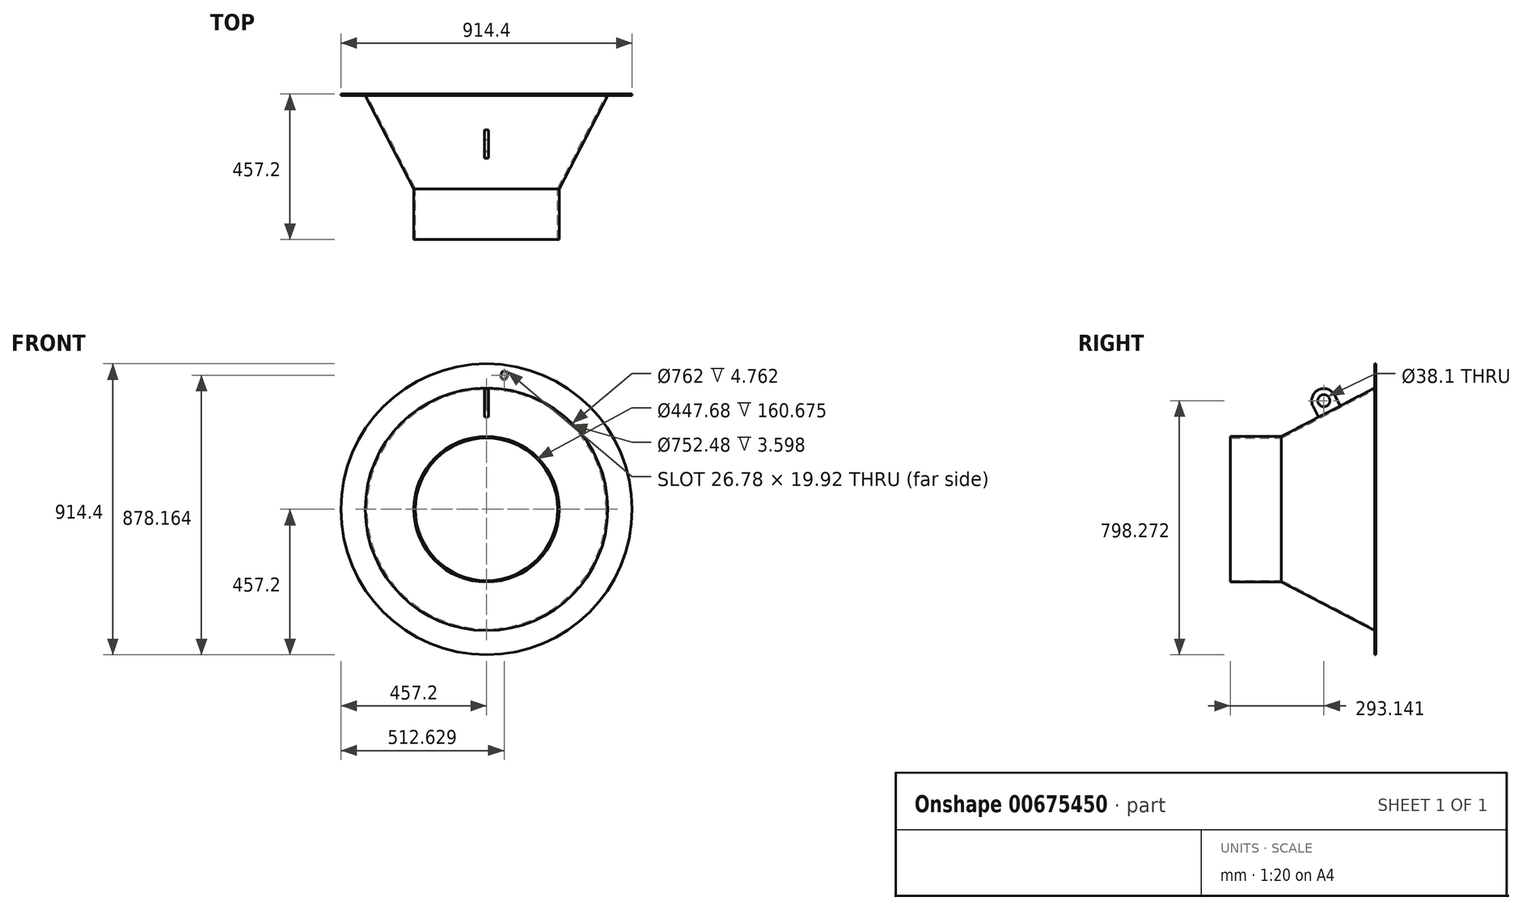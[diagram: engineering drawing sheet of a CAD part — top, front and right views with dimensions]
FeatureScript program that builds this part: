
annotation { "Feature Type Name" : "Feature", "Feature Type Description" : "" }
export const myFeature = defineFeature(function(context is Context, id is Id, definition is map)
    precondition{}
    {
        {
            var Q0;
            Q0=qCreatedBy(makeId("Front.planeOp"),FACE);
            var sketch = newSketch(context, id + "F0", { "sketchPlane" : qUnion([Q0])});
            skCircle(sketch, "E0", {"center": v(0, 0) * mm, "radius": 457.2 * mm});
            skCircle(sketch, "E1", {"center": v(0, 0) * mm, "radius": 428.63 * mm, "construction": true});
            skLineSegment(sketch, "E2", {"start": v(0, 0) * mm, "end": v(0, 611.06) * mm, "construction": true});
            skLineSegment(sketch, "E3", {"start": v(0, 0) * mm, "end": v(80.45, 611.06) * mm, "construction": true});
            skCircle(sketch, "E4", {"center": v(55.95, 424.96) * mm, "radius": 6.35 * mm});
            skCircle(sketch, "E5", {"center": v(0, 0) * mm, "radius": 381 * mm});
            skSolve(sketch);
        }
        {
            var Q0;
            Q0=qCreatedBy(makeId("Front.planeOp"),FACE);
            var sketch = newSketch(context, id + "F1", { "sketchPlane" : qUnion([Q0])});
            skCircle(sketch, "E6", {"center": v(0, 0) * mm, "radius": 420.69 * mm, "construction": true});
            skLineSegment(sketch, "E7.0", {"start": v(0, 0) * mm, "end": v(80.45, 611.06) * mm, "construction": true});
            skCircle(sketch, "E8", {"center": v(54.91, 417.09) * mm, "radius": 6.35 * mm});
            skSolve(sketch);
        }
        {
            var Q0;
            Q0=qCreatedBy(makeId("Front.planeOp"),FACE);
            var sketch = newSketch(context, id + "F2", { "sketchPlane" : qUnion([Q0])});
            skCircle(sketch, "E9.0", {"center": v(0, 0) * mm, "radius": 428.63 * mm, "construction": true});
            skCircle(sketch, "E10.0", {"center": v(0, 0) * mm, "radius": 420.69 * mm, "construction": true});
            skLineSegment(sketch, "E11.0", {"start": v(0, 0) * mm, "end": v(80.45, 611.06) * mm, "construction": true});
            skCircle(sketch, "E12", {"center": v(55.95, 424.96) * mm, "radius": 9.53 * mm});
            skCircle(sketch, "E13", {"center": v(54.91, 417.09) * mm, "radius": 9.53 * mm});
            skLineSegment(sketch, "E14", {"start": v(65.4, 423.71) * mm, "end": v(64.35, 415.85) * mm});
            skLineSegment(sketch, "E15", {"start": v(46.5, 426.2) * mm, "end": v(45.47, 418.33) * mm});
            skSolve(sketch);
        }
        {
            var Q0;
            Q0=qCreatedBy(makeId("Right.planeOp"),FACE);
            var sketch = newSketch(context, id + "F3", { "sketchPlane" : qUnion([Q0])});
            skLineSegment(sketch, "E16", {"start": v(190.49, 0) * mm, "end": v(-609.7, 0) * mm, "construction": true});
            skLineSegment(sketch, "E17", {"start": v(-4.76, 381) * mm, "end": v(-297.69, 228.6) * mm});
            skLineSegment(sketch, "E18", {"start": v(-297.69, 228.6) * mm, "end": v(-457.2, 228.6) * mm});
            skLineSegment(sketch, "E19", {"start": v(-457.2, 228.6) * mm, "end": v(-457.2, 0) * mm});
            skLineSegment(sketch, "E20", {"start": v(-457.2, 0) * mm, "end": v(0, 0) * mm});
            skLineSegment(sketch, "E21", {"start": v(0, 0) * mm, "end": v(0, 381) * mm});
            skLineSegment(sketch, "E22", {"start": v(-4.76, 381) * mm, "end": v(-4.76, 457.2) * mm});
            skLineSegment(sketch, "E23", {"start": v(-4.76, 457.2) * mm, "end": v(0, 457.2) * mm});
            skLineSegment(sketch, "E24", {"start": v(0, 381) * mm, "end": v(0, 457.2) * mm});
            skLineSegment(sketch, "E25", {"start": v(-4.76, 381) * mm, "end": v(0, 381) * mm});
            skLineSegment(sketch, "E26", {"start": v(0, 152.63) * mm, "end": v(-164.06, 152.63) * mm, "construction": true});
            skLineSegment(sketch, "E27", {"start": v(-164.06, 152.63) * mm, "end": v(-164.06, 434.36) * mm, "construction": true});
            skCircle(sketch, "E28", {"center": v(-164.06, 341.07) * mm, "radius": 38.1 * mm});
            skLineSegment(sketch, "E29", {"start": v(-130.26, 358.66) * mm, "end": v(-112.67, 324.86) * mm});
            skLineSegment(sketch, "E30", {"start": v(-197.86, 323.49) * mm, "end": v(-180.27, 289.69) * mm});
            skCircle(sketch, "E31", {"center": v(-164.06, 341.07) * mm, "radius": 19.05 * mm});
            skSolve(sketch);
        }
        {
            var Q0;
            Q0=makeQuery(id+"F3.imprint","IMPRINT",FACE,{"disambiguationData":[TD([[makeQuery(id+"F3.imprint","IMPRINT",EDGE,{"derivedFrom":sQuery(id+"F3.wireOp",EDGE,"E22")}),-1.0]])]});
            var Q1;
            Q1=sQuery(id+"F3.wireOp",EDGE,"E16");
            revolve(context, id + "F4", {"entities" : qUnion([Q0]), "axis" : qUnion([Q1]), "revolveType" : RevolveType.FULL});
        }
        {
            var Q0;
            Q0=makeQuery(id+"F3.imprint","IMPRINT",FACE,{"disambiguationData":[TD([[makeQuery(id+"F3.imprint","IMPRINT",EDGE,{"derivedFrom":sQuery(id+"F3.wireOp",EDGE,"E17")}),1.0]])]});
            var Q1;
            Q1=sQuery(id+"F3.wireOp",EDGE,"E16");
            revolve(context, id + "F5", {"entities" : qUnion([Q0]), "axis" : qUnion([Q1]), "revolveType" : RevolveType.FULL});
        }
        {
            var Q0;
            Q0=makeQuery(id+"F5.opRevolve","SWEPT_FACE",FACE,{"disambiguationData":[OSD([sQuery(id+"F3.wireOp",EDGE,"E19")])]});
            var Q1;
            Q1=makeQuery(id+"F5.opRevolve","SWEPT_FACE",FACE,{"disambiguationData":[OSD([sQuery(id+"F3.wireOp",EDGE,"E21")])]});
            shell(context, id + "F6", {"entities" : qUnion([Q0, Q1]), "thickness" : 4.76 * mm});
        }
        {
            var Q0;
            Q0=qCreatedBy(makeId("Front.planeOp"),FACE);
            var sketch = newSketch(context, id + "F7", { "sketchPlane" : qUnion([Q0])});
            skPoint(sketch, "E32.0", {"position": v(46.5, 426.2) * mm});
            skPoint(sketch, "E32.1", {"position": v(45.47, 418.33) * mm});
            skPoint(sketch, "E33.0", {"position": v(65.4, 423.71) * mm});
            skPoint(sketch, "E34.0", {"position": v(64.35, 415.85) * mm});
            skArc(sketch, "E35", {"start": v(65.4, 423.71) * mm, "mid": v(57.18, 434.35) * mm, "end": v(46.5, 426.2) * mm});
            skArc(sketch, "E36", {"start": v(45.47, 418.33) * mm, "mid": v(53.66, 407.58) * mm, "end": v(64.35, 415.85) * mm});
            skLineSegment(sketch, "E37", {"start": v(46.5, 426.2) * mm, "end": v(45.47, 418.33) * mm});
            skLineSegment(sketch, "E38", {"start": v(65.4, 423.71) * mm, "end": v(64.35, 415.85) * mm});
            skSolve(sketch);
        }
        {
            var Q0;
            Q0 = qSketchRegion(id + "F7", true);
            extrude(context, id + "F8", {"entities" : qUnion([Q0]), "operationType" : NewBodyOperationType.REMOVE, "endBound" : BoundingType.UP_TO_NEXT, "depth" : 25.4 * mm, "offsetDistance" : 25.4 * mm});
        }
        {
            var Q0;
            Q0=makeQuery(id+"F3.imprint","IMPRINT",FACE,{"disambiguationData":[TD([[makeQuery(id+"F3.imprint","IMPRINT",EDGE,{"derivedFrom":sQuery(id+"F3.wireOp",EDGE,"E31")}),-1.0]])]});
            var Q1;
            {var subQ0=sQuery(id+"F3.wireOp",EDGE,"E30");Q1=makeQuery(id+"F3.imprint","IMPRINT",FACE,{"disambiguationData":[TD([[makeQuery(id+"F3.imprint","IMPRINT",EDGE,{"derivedFrom":subQ0}),1.0]])]});}
            var Q2;
            {var subQ0=sQuery(id+"F3.wireOp",EDGE,"E29");Q2=makeQuery(id+"F3.imprint","IMPRINT",FACE,{"disambiguationData":[TD([[makeQuery(id+"F3.imprint","IMPRINT",EDGE,{"derivedFrom":subQ0}),-1.0]])]});}
            extrude(context, id + "F9", {"entities" : qUnion([Q0, Q1, Q2]), "endBound" : BoundingType.SYMMETRIC, "depth" : 12.7 * mm, "offsetDistance" : 25.4 * mm});
        }
    });
